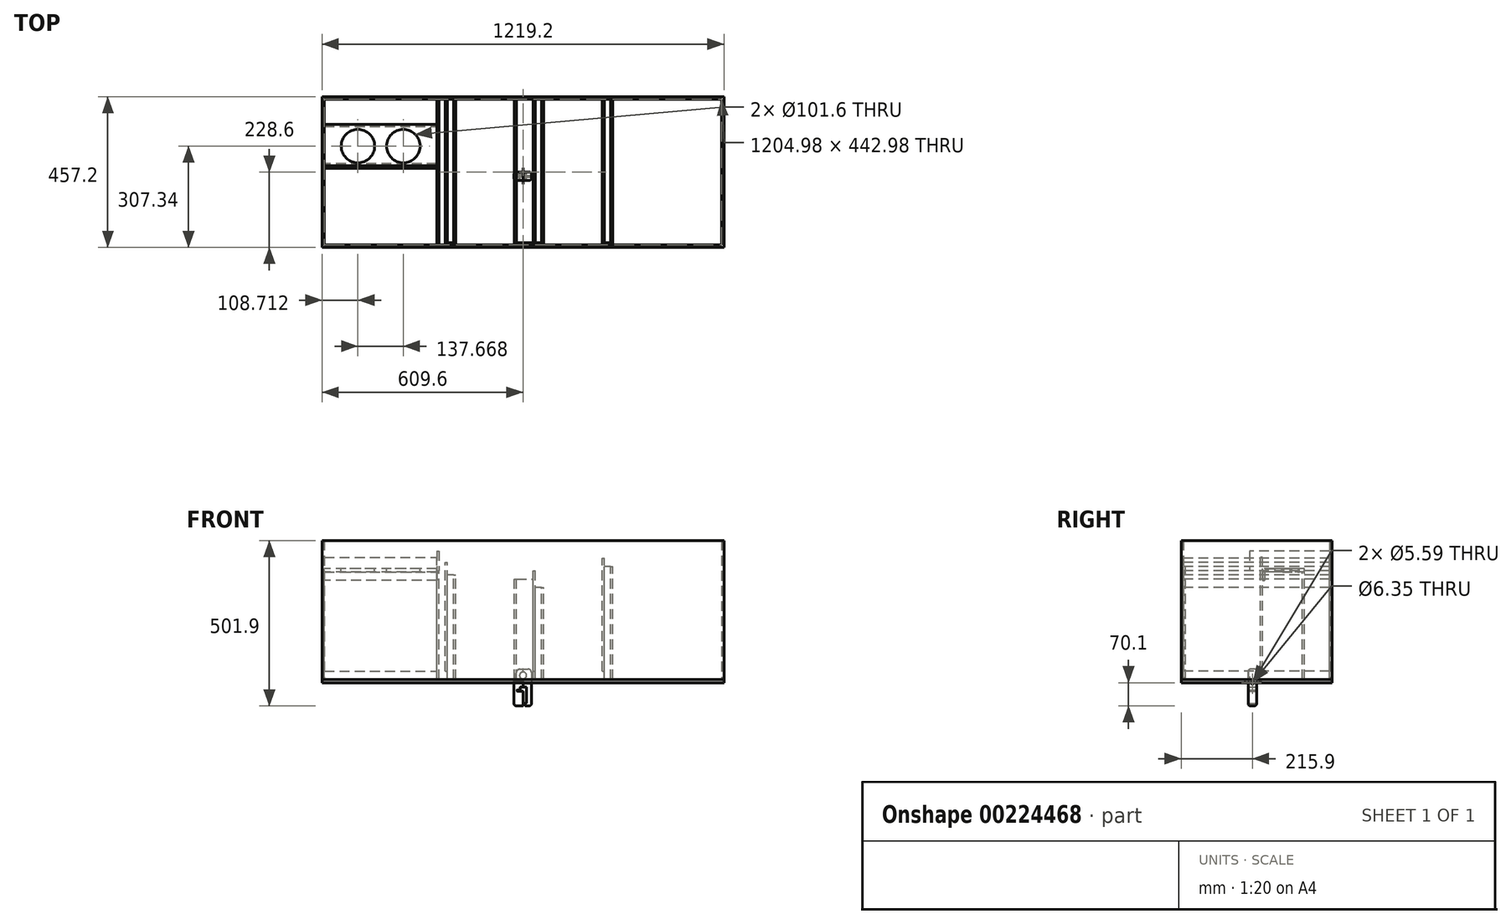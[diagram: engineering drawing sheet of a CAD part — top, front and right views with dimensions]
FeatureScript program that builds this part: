
annotation { "Feature Type Name" : "Feature", "Feature Type Description" : "" }
export const myFeature = defineFeature(function(context is Context, id is Id, definition is map)
    precondition{}
    {
        {
            var Q0;
            Q0=qCreatedBy(makeId("Top.planeOp"),FACE);
            var sketch = newSketch(context, id + "F0", { "sketchPlane" : qUnion([Q0])});
            skLineSegment(sketch, "E0.bottom", {"start": v(-609.6, 228.6) * mm, "end": v(609.6, 228.6) * mm});
            skLineSegment(sketch, "E0.top", {"start": v(-609.6, -228.6) * mm, "end": v(609.6, -228.6) * mm});
            skLineSegment(sketch, "E0.left", {"start": v(-609.6, 228.6) * mm, "end": v(-609.6, -228.6) * mm});
            skLineSegment(sketch, "E0.right", {"start": v(609.6, 228.6) * mm, "end": v(609.6, -228.6) * mm});
            skSolve(sketch);
        }
        {
            var Q0;
            Q0 = qSketchRegion(id + "F0", true);
            extrude(context, id + "F1", {"entities" : qUnion([Q0]), "depth" : 9.65 * mm});
        }
        {
            var Q0;
            Q0=makeQuery(id+"F1.opExtrude","CAP_FACE",FACE,{"disambiguationData":[OSD([sQuery(id+"F0.wireOp",EDGE,"E0.bottom"),sQuery(id+"F0.wireOp",EDGE,"E0.top"),sQuery(id+"F0.wireOp",EDGE,"E0.left"),sQuery(id+"F0.wireOp",EDGE,"E0.right")])],"isStart":false});
            var sketch = newSketch(context, id + "F2", { "sketchPlane" : qUnion([Q0])});
            skLineSegment(sketch, "E1.0", {"start": v(-602.49, 221.49) * mm, "end": v(602.49, 221.49) * mm});
            skLineSegment(sketch, "E1.1", {"start": v(-602.49, 221.49) * mm, "end": v(-602.49, -221.49) * mm});
            skLineSegment(sketch, "E1.2", {"start": v(-602.49, -221.49) * mm, "end": v(602.49, -221.49) * mm});
            skLineSegment(sketch, "E1.3", {"start": v(602.49, 221.49) * mm, "end": v(602.49, -221.49) * mm});
            skLineSegment(sketch, "E2", {"start": v(-609.6, 228.6) * mm, "end": v(609.6, 228.6) * mm});
            skLineSegment(sketch, "E3", {"start": v(609.6, 228.6) * mm, "end": v(609.6, -228.6) * mm});
            skLineSegment(sketch, "E4", {"start": v(609.6, -228.6) * mm, "end": v(-609.6, -228.6) * mm});
            skLineSegment(sketch, "E5", {"start": v(-609.6, -228.6) * mm, "end": v(-609.6, 228.6) * mm});
            skSolve(sketch);
        }
        {
            var Q0;
            Q0 = qSketchRegion(id + "F2", true);
            extrude(context, id + "F3", {"entities" : qUnion([Q0]), "depth" : 422.15 * mm});
        }
        {
            var Q0;
            Q0=makeQuery(id+"F3.opExtrude","CAP_FACE",FACE,{"disambiguationData":[OSD([sQuery(id+"F2.wireOp",EDGE,"E1.0"),sQuery(id+"F2.wireOp",EDGE,"E1.1"),sQuery(id+"F2.wireOp",EDGE,"E1.2"),sQuery(id+"F2.wireOp",EDGE,"E1.3"),sQuery(id+"F2.wireOp",EDGE,"E2"),sQuery(id+"F2.wireOp",EDGE,"E3"),sQuery(id+"F2.wireOp",EDGE,"E4"),sQuery(id+"F2.wireOp",EDGE,"E5")])],"isStart":false});
            var sketch = newSketch(context, id + "F4", { "sketchPlane" : qUnion([Q0])});
            skLineSegment(sketch, "E6", {"start": v(265.94, 221.49) * mm, "end": v(265.94, -221.49) * mm});
            skLineSegment(sketch, "E7", {"start": v(265.94, -221.49) * mm, "end": v(272.29, -221.49) * mm});
            skLineSegment(sketch, "E8", {"start": v(272.29, -221.49) * mm, "end": v(272.29, 221.49) * mm});
            skLineSegment(sketch, "E9", {"start": v(272.29, 221.49) * mm, "end": v(265.94, 221.49) * mm});
            skLineSegment(sketch, "E10", {"start": v(246.89, 221.49) * mm, "end": v(246.89, -221.49) * mm});
            skLineSegment(sketch, "E11", {"start": v(246.89, -221.49) * mm, "end": v(240.54, -221.49) * mm});
            skLineSegment(sketch, "E12", {"start": v(240.54, -221.49) * mm, "end": v(240.54, 221.49) * mm});
            skLineSegment(sketch, "E13", {"start": v(240.54, 221.49) * mm, "end": v(246.89, 221.49) * mm});
            skSolve(sketch);
        }
        {
            var Q0;
            Q0 = qSketchRegion(id + "F4", true);
            extrude(context, id + "F5", {"entities" : qUnion([Q0]), "oppositeDirection" : true, "depth" : 422.15 * mm});
        }
        {
            var Q0;
            Q0=makeQuery(id+"F5.opExtrude","CAP_FACE",FACE,{"disambiguationData":[OSD([sQuery(id+"F4.wireOp",EDGE,"E6"),sQuery(id+"F4.wireOp",EDGE,"E7"),sQuery(id+"F4.wireOp",EDGE,"E8"),sQuery(id+"F4.wireOp",EDGE,"E9")])],"isStart":true});
            var sketch = newSketch(context, id + "F6", { "sketchPlane" : qUnion([Q0])});
            skLineSegment(sketch, "E14.bottom", {"start": v(265.94, 221.49) * mm, "end": v(272.29, 221.49) * mm});
            skLineSegment(sketch, "E14.top", {"start": v(265.94, -221.49) * mm, "end": v(272.29, -221.49) * mm});
            skLineSegment(sketch, "E14.left", {"start": v(265.94, 221.49) * mm, "end": v(265.94, -221.49) * mm});
            skLineSegment(sketch, "E14.right", {"start": v(272.29, 221.49) * mm, "end": v(272.29, -221.49) * mm});
            skSolve(sketch);
        }
        {
            var Q0;
            Q0 = qSketchRegion(id + "F6", true);
            extrude(context, id + "F7", {"entities" : qUnion([Q0]), "operationType" : NewBodyOperationType.REMOVE, "oppositeDirection" : true, "depth" : 79.25 * mm});
        }
        {
            var Q0;
            Q0=makeQuery(id+"F5.opExtrude","CAP_FACE",FACE,{"disambiguationData":[OSD([sQuery(id+"F4.wireOp",EDGE,"E10"),sQuery(id+"F4.wireOp",EDGE,"E11"),sQuery(id+"F4.wireOp",EDGE,"E12"),sQuery(id+"F4.wireOp",EDGE,"E13")])],"isStart":true});
            var sketch = newSketch(context, id + "F8", { "sketchPlane" : qUnion([Q0])});
            skLineSegment(sketch, "E15.bottom", {"start": v(240.54, 221.49) * mm, "end": v(246.89, 221.49) * mm});
            skLineSegment(sketch, "E15.top", {"start": v(240.54, -221.49) * mm, "end": v(246.89, -221.49) * mm});
            skLineSegment(sketch, "E15.left", {"start": v(240.54, 221.49) * mm, "end": v(240.54, -221.49) * mm});
            skLineSegment(sketch, "E15.right", {"start": v(246.89, 221.49) * mm, "end": v(246.89, -221.49) * mm});
            skSolve(sketch);
        }
        {
            var Q0;
            Q0 = qSketchRegion(id + "F8", true);
            extrude(context, id + "F9", {"entities" : qUnion([Q0]), "operationType" : NewBodyOperationType.REMOVE, "oppositeDirection" : true, "depth" : 53.85 * mm});
        }
        {
            var Q0;
            Q0=makeQuery(id+"F5.opExtrude","CAP_FACE",FACE,{"disambiguationData":[OSD([sQuery(id+"F4.wireOp",EDGE,"E10"),sQuery(id+"F4.wireOp",EDGE,"E11"),sQuery(id+"F4.wireOp",EDGE,"E12"),sQuery(id+"F4.wireOp",EDGE,"E13")])],"isStart":false});
            var sketch = newSketch(context, id + "F10", { "sketchPlane" : qUnion([Q0])});
            skLineSegment(sketch, "E16.bottom", {"start": v(240.54, 221.49) * mm, "end": v(246.89, 221.49) * mm});
            skLineSegment(sketch, "E16.top", {"start": v(240.54, -221.49) * mm, "end": v(246.89, -221.49) * mm});
            skLineSegment(sketch, "E16.left", {"start": v(240.54, 221.49) * mm, "end": v(240.54, -221.49) * mm});
            skLineSegment(sketch, "E16.right", {"start": v(246.89, 221.49) * mm, "end": v(246.89, -221.49) * mm});
            skSolve(sketch);
        }
        {
            var Q0;
            Q0 = qSketchRegion(id + "F10", true);
            extrude(context, id + "F11", {"entities" : qUnion([Q0]), "operationType" : NewBodyOperationType.REMOVE, "oppositeDirection" : true, "depth" : 25.4 * mm});
        }
        {
            var Q0;
            Q0=makeQuery(id+"F3.opExtrude","CAP_FACE",FACE,{"disambiguationData":[OSD([sQuery(id+"F2.wireOp",EDGE,"E1.0"),sQuery(id+"F2.wireOp",EDGE,"E1.1"),sQuery(id+"F2.wireOp",EDGE,"E1.2"),sQuery(id+"F2.wireOp",EDGE,"E1.3"),sQuery(id+"F2.wireOp",EDGE,"E2"),sQuery(id+"F2.wireOp",EDGE,"E3"),sQuery(id+"F2.wireOp",EDGE,"E4"),sQuery(id+"F2.wireOp",EDGE,"E5")])],"isStart":false});
            var sketch = newSketch(context, id + "F12", { "sketchPlane" : qUnion([Q0])});
            skLineSegment(sketch, "E17.bottom", {"start": v(56.39, 221.49) * mm, "end": v(62.74, 221.49) * mm});
            skLineSegment(sketch, "E17.top", {"start": v(56.39, -221.49) * mm, "end": v(62.74, -221.49) * mm});
            skLineSegment(sketch, "E17.left", {"start": v(56.39, 221.49) * mm, "end": v(56.39, -221.49) * mm});
            skLineSegment(sketch, "E17.right", {"start": v(62.74, 221.49) * mm, "end": v(62.74, -221.49) * mm});
            skLineSegment(sketch, "E18.bottom", {"start": v(37.34, 221.49) * mm, "end": v(30.99, 221.49) * mm});
            skLineSegment(sketch, "E18.top", {"start": v(37.34, -221.49) * mm, "end": v(30.99, -221.49) * mm});
            skLineSegment(sketch, "E18.left", {"start": v(37.34, 221.49) * mm, "end": v(37.34, -221.49) * mm});
            skLineSegment(sketch, "E18.right", {"start": v(30.99, 221.49) * mm, "end": v(30.99, -221.49) * mm});
            skLineSegment(sketch, "E19.bottom", {"start": v(-26.16, 221.49) * mm, "end": v(-19.81, 221.49) * mm});
            skLineSegment(sketch, "E19.top", {"start": v(-26.16, -221.49) * mm, "end": v(-19.81, -221.49) * mm});
            skLineSegment(sketch, "E19.left", {"start": v(-26.16, 221.49) * mm, "end": v(-26.16, -221.49) * mm});
            skLineSegment(sketch, "E19.right", {"start": v(-19.81, 221.49) * mm, "end": v(-19.81, -221.49) * mm});
            skLineSegment(sketch, "E20.bottom", {"start": v(-210.31, 221.49) * mm, "end": v(-203.96, 221.49) * mm});
            skLineSegment(sketch, "E20.top", {"start": v(-210.31, -221.49) * mm, "end": v(-203.96, -221.49) * mm});
            skLineSegment(sketch, "E20.left", {"start": v(-210.31, 221.49) * mm, "end": v(-210.31, -221.49) * mm});
            skLineSegment(sketch, "E20.right", {"start": v(-203.96, 221.49) * mm, "end": v(-203.96, -221.49) * mm});
            skLineSegment(sketch, "E21.bottom", {"start": v(-235.71, 221.49) * mm, "end": v(-229.36, 221.49) * mm});
            skLineSegment(sketch, "E21.top", {"start": v(-235.71, -221.49) * mm, "end": v(-229.36, -221.49) * mm});
            skLineSegment(sketch, "E21.left", {"start": v(-235.71, 221.49) * mm, "end": v(-235.71, -221.49) * mm});
            skLineSegment(sketch, "E21.right", {"start": v(-229.36, 221.49) * mm, "end": v(-229.36, -221.49) * mm});
            skLineSegment(sketch, "E22.bottom", {"start": v(-261.11, 221.49) * mm, "end": v(-254.76, 221.49) * mm});
            skLineSegment(sketch, "E22.top", {"start": v(-261.11, -221.49) * mm, "end": v(-254.76, -221.49) * mm});
            skLineSegment(sketch, "E22.left", {"start": v(-261.11, 221.49) * mm, "end": v(-261.11, -221.49) * mm});
            skLineSegment(sketch, "E22.right", {"start": v(-254.76, 221.49) * mm, "end": v(-254.76, -221.49) * mm});
            skSolve(sketch);
        }
        {
            var Q0;
            Q0 = qSketchRegion(id + "F12", true);
            extrude(context, id + "F13", {"entities" : qUnion([Q0]), "oppositeDirection" : true, "depth" : 422.15 * mm});
        }
        {
            var Q0;
            Q0=makeQuery(id+"F13.opExtrude","CAP_FACE",FACE,{"disambiguationData":[OSD([sQuery(id+"F12.wireOp",EDGE,"E17.bottom"),sQuery(id+"F12.wireOp",EDGE,"E17.top"),sQuery(id+"F12.wireOp",EDGE,"E17.left"),sQuery(id+"F12.wireOp",EDGE,"E17.right")])],"isStart":true});
            var sketch = newSketch(context, id + "F14", { "sketchPlane" : qUnion([Q0])});
            skLineSegment(sketch, "E23.bottom", {"start": v(56.39, 221.49) * mm, "end": v(62.74, 221.49) * mm});
            skLineSegment(sketch, "E23.top", {"start": v(56.39, -221.49) * mm, "end": v(62.74, -221.49) * mm});
            skLineSegment(sketch, "E23.left", {"start": v(56.39, 221.49) * mm, "end": v(56.39, -221.49) * mm});
            skLineSegment(sketch, "E23.right", {"start": v(62.74, 221.49) * mm, "end": v(62.74, -221.49) * mm});
            skSolve(sketch);
        }
        {
            var Q0;
            Q0 = qSketchRegion(id + "F14", true);
            extrude(context, id + "F15", {"entities" : qUnion([Q0]), "operationType" : NewBodyOperationType.REMOVE, "oppositeDirection" : true, "depth" : 142.75 * mm});
        }
        {
            var Q0;
            Q0=makeQuery(id+"F13.opExtrude","CAP_FACE",FACE,{"disambiguationData":[OSD([sQuery(id+"F12.wireOp",EDGE,"E18.bottom"),sQuery(id+"F12.wireOp",EDGE,"E18.top"),sQuery(id+"F12.wireOp",EDGE,"E18.left"),sQuery(id+"F12.wireOp",EDGE,"E18.right")])],"isStart":true});
            var sketch = newSketch(context, id + "F16", { "sketchPlane" : qUnion([Q0])});
            skLineSegment(sketch, "E24.bottom", {"start": v(30.99, 221.49) * mm, "end": v(37.34, 221.49) * mm});
            skLineSegment(sketch, "E24.top", {"start": v(30.99, -221.49) * mm, "end": v(37.34, -221.49) * mm});
            skLineSegment(sketch, "E24.left", {"start": v(30.99, 221.49) * mm, "end": v(30.99, -221.49) * mm});
            skLineSegment(sketch, "E24.right", {"start": v(37.34, 221.49) * mm, "end": v(37.34, -221.49) * mm});
            skSolve(sketch);
        }
        {
            var Q0;
            Q0 = qSketchRegion(id + "F16", true);
            extrude(context, id + "F17", {"entities" : qUnion([Q0]), "operationType" : NewBodyOperationType.REMOVE, "oppositeDirection" : true, "depth" : 91.95 * mm});
        }
        {
            var Q0;
            Q0=makeQuery(id+"F13.opExtrude","CAP_FACE",FACE,{"disambiguationData":[OSD([sQuery(id+"F12.wireOp",EDGE,"E19.bottom"),sQuery(id+"F12.wireOp",EDGE,"E19.top"),sQuery(id+"F12.wireOp",EDGE,"E19.left"),sQuery(id+"F12.wireOp",EDGE,"E19.right")])],"isStart":true});
            var sketch = newSketch(context, id + "F18", { "sketchPlane" : qUnion([Q0])});
            skLineSegment(sketch, "E25.bottom", {"start": v(-26.16, 221.49) * mm, "end": v(-19.81, 221.49) * mm});
            skLineSegment(sketch, "E25.top", {"start": v(-26.16, -221.49) * mm, "end": v(-19.81, -221.49) * mm});
            skLineSegment(sketch, "E25.left", {"start": v(-26.16, 221.49) * mm, "end": v(-26.16, -221.49) * mm});
            skLineSegment(sketch, "E25.right", {"start": v(-19.81, 221.49) * mm, "end": v(-19.81, -221.49) * mm});
            skSolve(sketch);
        }
        {
            var Q0;
            Q0 = qSketchRegion(id + "F18", true);
            extrude(context, id + "F19", {"entities" : qUnion([Q0]), "operationType" : NewBodyOperationType.REMOVE, "oppositeDirection" : true, "depth" : 117.35 * mm});
        }
        {
            var Q0;
            Q0=makeQuery(id+"F13.opExtrude","CAP_FACE",FACE,{"disambiguationData":[OSD([sQuery(id+"F12.wireOp",EDGE,"E18.bottom"),sQuery(id+"F12.wireOp",EDGE,"E18.top"),sQuery(id+"F12.wireOp",EDGE,"E18.left"),sQuery(id+"F12.wireOp",EDGE,"E18.right")])],"isStart":false});
            var sketch = newSketch(context, id + "F20", { "sketchPlane" : qUnion([Q0])});
            skLineSegment(sketch, "E26.bottom", {"start": v(30.99, 221.49) * mm, "end": v(37.34, 221.49) * mm});
            skLineSegment(sketch, "E26.top", {"start": v(30.99, -221.49) * mm, "end": v(37.34, -221.49) * mm});
            skLineSegment(sketch, "E26.left", {"start": v(30.99, 221.49) * mm, "end": v(30.99, -221.49) * mm});
            skLineSegment(sketch, "E26.right", {"start": v(37.34, 221.49) * mm, "end": v(37.34, -221.49) * mm});
            skSolve(sketch);
        }
        {
            var Q0;
            Q0 = qSketchRegion(id + "F20", true);
            extrude(context, id + "F21", {"entities" : qUnion([Q0]), "operationType" : NewBodyOperationType.REMOVE, "oppositeDirection" : true, "depth" : 25.4 * mm});
        }
        {
            var Q0;
            Q0=makeQuery(id+"F13.opExtrude","CAP_FACE",FACE,{"disambiguationData":[OSD([sQuery(id+"F12.wireOp",EDGE,"E20.bottom"),sQuery(id+"F12.wireOp",EDGE,"E20.top"),sQuery(id+"F12.wireOp",EDGE,"E20.left"),sQuery(id+"F12.wireOp",EDGE,"E20.right")])],"isStart":true});
            var sketch = newSketch(context, id + "F22", { "sketchPlane" : qUnion([Q0])});
            skLineSegment(sketch, "E27.bottom", {"start": v(-210.31, 221.49) * mm, "end": v(-203.96, 221.49) * mm});
            skLineSegment(sketch, "E27.top", {"start": v(-210.31, -221.49) * mm, "end": v(-203.96, -221.49) * mm});
            skLineSegment(sketch, "E27.left", {"start": v(-210.31, 221.49) * mm, "end": v(-210.31, -221.49) * mm});
            skLineSegment(sketch, "E27.right", {"start": v(-203.96, 221.49) * mm, "end": v(-203.96, -221.49) * mm});
            skSolve(sketch);
        }
        {
            var Q0;
            Q0 = qSketchRegion(id + "F22", true);
            extrude(context, id + "F23", {"entities" : qUnion([Q0]), "operationType" : NewBodyOperationType.REMOVE, "oppositeDirection" : true, "depth" : 104.65 * mm});
        }
        {
            var Q0;
            Q0=makeQuery(id+"F13.opExtrude","CAP_FACE",FACE,{"disambiguationData":[OSD([sQuery(id+"F12.wireOp",EDGE,"E21.bottom"),sQuery(id+"F12.wireOp",EDGE,"E21.top"),sQuery(id+"F12.wireOp",EDGE,"E21.left"),sQuery(id+"F12.wireOp",EDGE,"E21.right")])],"isStart":true});
            var sketch = newSketch(context, id + "F24", { "sketchPlane" : qUnion([Q0])});
            skLineSegment(sketch, "E28.bottom", {"start": v(-235.71, 221.49) * mm, "end": v(-229.36, 221.49) * mm});
            skLineSegment(sketch, "E28.top", {"start": v(-235.71, -221.49) * mm, "end": v(-229.36, -221.49) * mm});
            skLineSegment(sketch, "E28.left", {"start": v(-235.71, 221.49) * mm, "end": v(-235.71, -221.49) * mm});
            skLineSegment(sketch, "E28.right", {"start": v(-229.36, 221.49) * mm, "end": v(-229.36, -221.49) * mm});
            skSolve(sketch);
        }
        {
            var Q0;
            Q0 = qSketchRegion(id + "F24", true);
            extrude(context, id + "F25", {"entities" : qUnion([Q0]), "operationType" : NewBodyOperationType.REMOVE, "oppositeDirection" : true, "depth" : 66.55 * mm});
        }
        {
            var Q0;
            Q0=makeQuery(id+"F13.opExtrude","CAP_FACE",FACE,{"disambiguationData":[OSD([sQuery(id+"F12.wireOp",EDGE,"E22.bottom"),sQuery(id+"F12.wireOp",EDGE,"E22.top"),sQuery(id+"F12.wireOp",EDGE,"E22.left"),sQuery(id+"F12.wireOp",EDGE,"E22.right")])],"isStart":true});
            var sketch = newSketch(context, id + "F26", { "sketchPlane" : qUnion([Q0])});
            skLineSegment(sketch, "E29.bottom", {"start": v(-261.11, 221.49) * mm, "end": v(-254.76, 221.49) * mm});
            skLineSegment(sketch, "E29.top", {"start": v(-261.11, -221.49) * mm, "end": v(-254.76, -221.49) * mm});
            skLineSegment(sketch, "E29.left", {"start": v(-261.11, 221.49) * mm, "end": v(-261.11, -221.49) * mm});
            skLineSegment(sketch, "E29.right", {"start": v(-254.76, 221.49) * mm, "end": v(-254.76, -221.49) * mm});
            skSolve(sketch);
        }
        {
            var Q0;
            Q0 = qSketchRegion(id + "F26", true);
            extrude(context, id + "F27", {"entities" : qUnion([Q0]), "operationType" : NewBodyOperationType.REMOVE, "oppositeDirection" : true, "depth" : 91.95 * mm});
        }
        {
            var Q0;
            Q0=makeQuery(id+"F3.opExtrude","CAP_FACE",FACE,{"disambiguationData":[OSD([sQuery(id+"F2.wireOp",EDGE,"E1.0"),sQuery(id+"F2.wireOp",EDGE,"E1.1"),sQuery(id+"F2.wireOp",EDGE,"E1.2"),sQuery(id+"F2.wireOp",EDGE,"E1.3"),sQuery(id+"F2.wireOp",EDGE,"E2"),sQuery(id+"F2.wireOp",EDGE,"E3"),sQuery(id+"F2.wireOp",EDGE,"E4"),sQuery(id+"F2.wireOp",EDGE,"E5")])],"isStart":false});
            var sketch = newSketch(context, id + "F28", { "sketchPlane" : qUnion([Q0])});
            skLineSegment(sketch, "E30.bottom", {"start": v(-602.49, 145.29) * mm, "end": v(-261.5, 145.29) * mm});
            skLineSegment(sketch, "E30.top", {"start": v(-602.49, 138.94) * mm, "end": v(-261.5, 138.94) * mm});
            skLineSegment(sketch, "E30.left", {"start": v(-602.49, 145.29) * mm, "end": v(-602.49, 138.94) * mm});
            skLineSegment(sketch, "E30.right", {"start": v(-261.5, 145.29) * mm, "end": v(-261.5, 138.94) * mm});
            skLineSegment(sketch, "E31.bottom", {"start": v(-602.49, 18.29) * mm, "end": v(-261.5, 18.29) * mm});
            skLineSegment(sketch, "E31.top", {"start": v(-602.49, 11.94) * mm, "end": v(-261.5, 11.94) * mm});
            skLineSegment(sketch, "E31.left", {"start": v(-602.49, 18.29) * mm, "end": v(-602.49, 11.94) * mm});
            skLineSegment(sketch, "E31.right", {"start": v(-261.5, 18.29) * mm, "end": v(-261.5, 11.94) * mm});
            skSolve(sketch);
        }
        {
            var Q0;
            Q0 = qSketchRegion(id + "F28", true);
            extrude(context, id + "F29", {"entities" : qUnion([Q0]), "oppositeDirection" : true, "depth" : 422.15 * mm});
        }
        {
            var Q0;
            Q0=makeQuery(id+"F13.opExtrude","CAP_FACE",FACE,{"disambiguationData":[OSD([sQuery(id+"F12.wireOp",EDGE,"E21.bottom"),sQuery(id+"F12.wireOp",EDGE,"E21.top"),sQuery(id+"F12.wireOp",EDGE,"E21.left"),sQuery(id+"F12.wireOp",EDGE,"E21.right")])],"isStart":false});
            var sketch = newSketch(context, id + "F30", { "sketchPlane" : qUnion([Q0])});
            skLineSegment(sketch, "E32.bottom", {"start": v(-235.71, 221.49) * mm, "end": v(-229.36, 221.49) * mm});
            skLineSegment(sketch, "E32.top", {"start": v(-235.71, -221.49) * mm, "end": v(-229.36, -221.49) * mm});
            skLineSegment(sketch, "E32.left", {"start": v(-235.71, 221.49) * mm, "end": v(-235.71, -221.49) * mm});
            skLineSegment(sketch, "E32.right", {"start": v(-229.36, 221.49) * mm, "end": v(-229.36, -221.49) * mm});
            skSolve(sketch);
        }
        {
            var Q0;
            Q0 = qSketchRegion(id + "F30", true);
            extrude(context, id + "F31", {"entities" : qUnion([Q0]), "operationType" : NewBodyOperationType.REMOVE, "oppositeDirection" : true, "depth" : 25.4 * mm});
        }
        {
            var Q0;
            Q0=makeQuery(id+"F29.opExtrude","CAP_FACE",FACE,{"disambiguationData":[OSD([sQuery(id+"F28.wireOp",EDGE,"E31.bottom"),sQuery(id+"F28.wireOp",EDGE,"E31.top"),sQuery(id+"F28.wireOp",EDGE,"E31.left"),sQuery(id+"F28.wireOp",EDGE,"E31.right")])],"isStart":false});
            var sketch = newSketch(context, id + "F32", { "sketchPlane" : qUnion([Q0])});
            skLineSegment(sketch, "E33.bottom", {"start": v(-602.49, -11.94) * mm, "end": v(-261.5, -11.94) * mm});
            skLineSegment(sketch, "E33.top", {"start": v(-602.49, -18.29) * mm, "end": v(-261.5, -18.29) * mm});
            skLineSegment(sketch, "E33.left", {"start": v(-602.49, -11.94) * mm, "end": v(-602.49, -18.29) * mm});
            skLineSegment(sketch, "E33.right", {"start": v(-261.5, -11.94) * mm, "end": v(-261.5, -18.29) * mm});
            skSolve(sketch);
        }
        {
            var Q0;
            Q0 = qSketchRegion(id + "F32", true);
            extrude(context, id + "F33", {"entities" : qUnion([Q0]), "operationType" : NewBodyOperationType.REMOVE, "oppositeDirection" : true, "depth" : 25.4 * mm});
        }
        {
            var Q0;
            Q0=makeQuery(id+"F29.opExtrude","CAP_FACE",FACE,{"disambiguationData":[OSD([sQuery(id+"F28.wireOp",EDGE,"E30.bottom"),sQuery(id+"F28.wireOp",EDGE,"E30.top"),sQuery(id+"F28.wireOp",EDGE,"E30.left"),sQuery(id+"F28.wireOp",EDGE,"E30.right")])],"isStart":true});
            var sketch = newSketch(context, id + "F34", { "sketchPlane" : qUnion([Q0])});
            skLineSegment(sketch, "E34.bottom", {"start": v(-602.49, 145.29) * mm, "end": v(-261.5, 145.29) * mm});
            skLineSegment(sketch, "E34.top", {"start": v(-602.49, 138.94) * mm, "end": v(-261.5, 138.94) * mm});
            skLineSegment(sketch, "E34.left", {"start": v(-602.49, 145.29) * mm, "end": v(-602.49, 138.94) * mm});
            skLineSegment(sketch, "E34.right", {"start": v(-261.5, 145.29) * mm, "end": v(-261.5, 138.94) * mm});
            skSolve(sketch);
        }
        {
            var Q0;
            Q0 = qSketchRegion(id + "F34", true);
            extrude(context, id + "F35", {"entities" : qUnion([Q0]), "operationType" : NewBodyOperationType.REMOVE, "oppositeDirection" : true, "depth" : 95.25 * mm});
        }
        {
            var Q0;
            Q0=makeQuery(id+"F29.opExtrude","CAP_FACE",FACE,{"disambiguationData":[OSD([sQuery(id+"F28.wireOp",EDGE,"E31.bottom"),sQuery(id+"F28.wireOp",EDGE,"E31.top"),sQuery(id+"F28.wireOp",EDGE,"E31.left"),sQuery(id+"F28.wireOp",EDGE,"E31.right")])],"isStart":true});
            var sketch = newSketch(context, id + "F36", { "sketchPlane" : qUnion([Q0])});
            skLineSegment(sketch, "E35.bottom", {"start": v(-602.49, 18.29) * mm, "end": v(-261.5, 18.29) * mm});
            skLineSegment(sketch, "E35.top", {"start": v(-602.49, 11.94) * mm, "end": v(-261.5, 11.94) * mm});
            skLineSegment(sketch, "E35.left", {"start": v(-602.49, 18.29) * mm, "end": v(-602.49, 11.94) * mm});
            skLineSegment(sketch, "E35.right", {"start": v(-261.5, 18.29) * mm, "end": v(-261.5, 11.94) * mm});
            skSolve(sketch);
        }
        {
            var Q0;
            Q0 = qSketchRegion(id + "F36", true);
            extrude(context, id + "F37", {"entities" : qUnion([Q0]), "operationType" : NewBodyOperationType.REMOVE, "oppositeDirection" : true, "depth" : 50.8 * mm});
        }
        {
            var Q0;
            Q0=makeQuery(id+"F27.boolean.opBoolean","COPY",FACE,{"derivedFrom":makeQuery(id+"F27.opExtrude","CAP_FACE",FACE,{"disambiguationData":[OSD([sQuery(id+"F26.wireOp",EDGE,"E29.bottom"),sQuery(id+"F26.wireOp",EDGE,"E29.top"),sQuery(id+"F26.wireOp",EDGE,"E29.left"),sQuery(id+"F26.wireOp",EDGE,"E29.right")])],"isStart":false})});
            var sketch = newSketch(context, id + "F38", { "sketchPlane" : qUnion([Q0])});
            skLineSegment(sketch, "E36.bottom", {"start": v(-261.11, 221.49) * mm, "end": v(-254.76, 221.49) * mm});
            skLineSegment(sketch, "E36.top", {"start": v(-261.11, -21.6) * mm, "end": v(-254.76, -21.6) * mm});
            skLineSegment(sketch, "E36.left", {"start": v(-261.11, 221.49) * mm, "end": v(-261.11, -21.6) * mm});
            skLineSegment(sketch, "E36.right", {"start": v(-254.76, 221.49) * mm, "end": v(-254.76, -21.6) * mm});
            skSolve(sketch);
        }
        {
            var Q0;
            Q0 = qSketchRegion(id + "F38", true);
            extrude(context, id + "F39", {"entities" : qUnion([Q0]), "depth" : 60.45 * mm});
        }
        {
            var Q0;
            Q0=makeQuery(id+"F29.opExtrude","SWEPT_FACE",FACE,{"disambiguationData":[OSD([sQuery(id+"F28.wireOp",EDGE,"E30.left")])]});
            var sketch = newSketch(context, id + "F40", { "sketchPlane" : qUnion([Q0])});
            skLineSegment(sketch, "E37.bottom", {"start": v(-145.29, 336.55) * mm, "end": v(-18.35, 336.55) * mm});
            skLineSegment(sketch, "E37.top", {"start": v(-145.29, 346.2) * mm, "end": v(-18.35, 346.2) * mm});
            skLineSegment(sketch, "E37.left", {"start": v(-145.29, 336.55) * mm, "end": v(-145.29, 346.2) * mm});
            skLineSegment(sketch, "E37.right", {"start": v(-18.35, 336.55) * mm, "end": v(-18.35, 346.2) * mm});
            skSolve(sketch);
        }
        {
            var Q0;
            Q0 = qSketchRegion(id + "F40", true);
            extrude(context, id + "F41", {"entities" : qUnion([Q0]), "oppositeDirection" : true, "depth" : 340.87 * mm});
        }
        {
            var Q0;
            Q0=makeQuery(id+"F41.opExtrude","SWEPT_FACE",FACE,{"disambiguationData":[OSD([sQuery(id+"F40.wireOp",EDGE,"E37.top")])]});
            var sketch = newSketch(context, id + "F42", { "sketchPlane" : qUnion([Q0])});
            skCircle(sketch, "E38", {"center": v(-500.89, 78.74) * mm, "radius": 50.8 * mm});
            skCircle(sketch, "E39", {"center": v(-363.22, 78.74) * mm, "radius": 50.8 * mm});
            skSolve(sketch);
        }
        {
            var Q0;
            Q0 = qSketchRegion(id + "F42", true);
            extrude(context, id + "F43", {"entities" : qUnion([Q0]), "operationType" : NewBodyOperationType.REMOVE, "oppositeDirection" : true, "depth" : 25.4 * mm});
        }
        {
            var Q0;
            Q0=makeQuery(id+"F23.boolean.opBoolean","COPY",FACE,{"derivedFrom":makeQuery(id+"F23.opExtrude","CAP_FACE",FACE,{"disambiguationData":[OSD([sQuery(id+"F22.wireOp",EDGE,"E27.bottom"),sQuery(id+"F22.wireOp",EDGE,"E27.top"),sQuery(id+"F22.wireOp",EDGE,"E27.left"),sQuery(id+"F22.wireOp",EDGE,"E27.right")])],"isStart":false})});
            var sketch = newSketch(context, id + "F44", { "sketchPlane" : qUnion([Q0])});
            skLineSegment(sketch, "E40.bottom", {"start": v(-210.31, -221.49) * mm, "end": v(-229.36, -221.49) * mm});
            skLineSegment(sketch, "E40.top", {"start": v(-210.31, -215.14) * mm, "end": v(-229.36, -215.14) * mm});
            skLineSegment(sketch, "E40.left", {"start": v(-210.31, -221.49) * mm, "end": v(-210.31, -215.14) * mm});
            skLineSegment(sketch, "E40.right", {"start": v(-229.36, -221.49) * mm, "end": v(-229.36, -215.14) * mm});
            skSolve(sketch);
        }
        {
            var Q0;
            Q0 = qSketchRegion(id + "F44", true);
            extrude(context, id + "F45", {"entities" : qUnion([Q0]), "oppositeDirection" : true, "depth" : 317.5 * mm});
        }
        {
            var Q0;
            Q0=makeQuery(id+"F7.boolean.opBoolean","COPY",FACE,{"derivedFrom":makeQuery(id+"F7.opExtrude","CAP_FACE",FACE,{"disambiguationData":[OSD([sQuery(id+"F6.wireOp",EDGE,"E14.bottom"),sQuery(id+"F6.wireOp",EDGE,"E14.top"),sQuery(id+"F6.wireOp",EDGE,"E14.left"),sQuery(id+"F6.wireOp",EDGE,"E14.right")])],"isStart":false})});
            var sketch = newSketch(context, id + "F46", { "sketchPlane" : qUnion([Q0])});
            skLineSegment(sketch, "E41.bottom", {"start": v(265.94, -221.49) * mm, "end": v(246.89, -221.49) * mm});
            skLineSegment(sketch, "E41.top", {"start": v(265.94, -215.14) * mm, "end": v(246.89, -215.14) * mm});
            skLineSegment(sketch, "E41.left", {"start": v(265.94, -221.49) * mm, "end": v(265.94, -215.14) * mm});
            skLineSegment(sketch, "E41.right", {"start": v(246.89, -221.49) * mm, "end": v(246.89, -215.14) * mm});
            skSolve(sketch);
        }
        {
            var Q0;
            Q0 = qSketchRegion(id + "F46", true);
            extrude(context, id + "F47", {"entities" : qUnion([Q0]), "oppositeDirection" : true, "depth" : 342.9 * mm});
        }
        {
            var Q0;
            Q0=makeQuery(id+"F15.boolean.opBoolean","COPY",FACE,{"derivedFrom":makeQuery(id+"F15.opExtrude","CAP_FACE",FACE,{"disambiguationData":[OSD([sQuery(id+"F14.wireOp",EDGE,"E23.bottom"),sQuery(id+"F14.wireOp",EDGE,"E23.top"),sQuery(id+"F14.wireOp",EDGE,"E23.left"),sQuery(id+"F14.wireOp",EDGE,"E23.right")])],"isStart":false})});
            var sketch = newSketch(context, id + "F48", { "sketchPlane" : qUnion([Q0])});
            skLineSegment(sketch, "E42.bottom", {"start": v(56.39, -221.49) * mm, "end": v(37.34, -221.49) * mm});
            skLineSegment(sketch, "E42.top", {"start": v(56.39, -215.14) * mm, "end": v(37.34, -215.14) * mm});
            skLineSegment(sketch, "E42.left", {"start": v(56.39, -221.49) * mm, "end": v(56.39, -215.14) * mm});
            skLineSegment(sketch, "E42.right", {"start": v(37.34, -221.49) * mm, "end": v(37.34, -215.14) * mm});
            skSolve(sketch);
        }
        {
            var Q0;
            Q0 = qSketchRegion(id + "F48", true);
            extrude(context, id + "F49", {"entities" : qUnion([Q0]), "oppositeDirection" : true, "depth" : 279.4 * mm});
        }
        {
            var Q0;
            Q0=makeQuery(id+"F19.boolean.opBoolean","COPY",FACE,{"derivedFrom":makeQuery(id+"F19.opExtrude","CAP_FACE",FACE,{"disambiguationData":[OSD([sQuery(id+"F18.wireOp",EDGE,"E25.bottom"),sQuery(id+"F18.wireOp",EDGE,"E25.top"),sQuery(id+"F18.wireOp",EDGE,"E25.left"),sQuery(id+"F18.wireOp",EDGE,"E25.right")])],"isStart":false})});
            var sketch = newSketch(context, id + "F50", { "sketchPlane" : qUnion([Q0])});
            skLineSegment(sketch, "E43.bottom", {"start": v(-19.81, -221.49) * mm, "end": v(30.99, -221.49) * mm});
            skLineSegment(sketch, "E43.top", {"start": v(-19.81, -215.14) * mm, "end": v(30.99, -215.14) * mm});
            skLineSegment(sketch, "E43.left", {"start": v(-19.81, -221.49) * mm, "end": v(-19.81, -215.14) * mm});
            skLineSegment(sketch, "E43.right", {"start": v(30.99, -221.49) * mm, "end": v(30.99, -215.14) * mm});
            skSolve(sketch);
        }
        {
            var Q0;
            Q0 = qSketchRegion(id + "F50", true);
            extrude(context, id + "F51", {"entities" : qUnion([Q0]), "oppositeDirection" : true, "depth" : 304.8 * mm});
        }
        {
            var Q0;
            Q0=makeQuery(id+"F41.opExtrude","CAP_FACE",FACE,{"disambiguationData":[OSD([sQuery(id+"F40.wireOp",EDGE,"E37.bottom"),sQuery(id+"F40.wireOp",EDGE,"E37.top"),sQuery(id+"F40.wireOp",EDGE,"E37.left"),sQuery(id+"F40.wireOp",EDGE,"E37.right")])],"isStart":true});
            var sketch = newSketch(context, id + "F52", { "sketchPlane" : qUnion([Q0])});
            skLineSegment(sketch, "E44.bottom", {"start": v(-18.35, 336.55) * mm, "end": v(-24.7, 336.55) * mm});
            skLineSegment(sketch, "E44.top", {"start": v(-18.35, 311.15) * mm, "end": v(-24.7, 311.15) * mm});
            skLineSegment(sketch, "E44.left", {"start": v(-18.35, 336.55) * mm, "end": v(-18.35, 311.15) * mm});
            skLineSegment(sketch, "E44.right", {"start": v(-24.7, 336.55) * mm, "end": v(-24.7, 311.15) * mm});
            skSolve(sketch);
        }
        {
            var Q0;
            Q0 = qSketchRegion(id + "F52", true);
            extrude(context, id + "F53", {"entities" : qUnion([Q0]), "oppositeDirection" : true, "depth" : 340.87 * mm});
        }
        {
            var Q0;
            Q0=qCreatedBy(makeId("Front.planeOp"),FACE);
            var sketch = newSketch(context, id + "F54", { "sketchPlane" : qUnion([Q0])});
            skLineSegment(sketch, "E45.bottom", {"start": v(-9.53, 41.15) * mm, "end": v(15.87, 41.15) * mm});
            skLineSegment(sketch, "E45.top", {"start": v(-27.3, -69.85) * mm, "end": v(0, -69.85) * mm});
            skLineSegment(sketch, "E45.left", {"start": v(-27.3, 15.9) * mm, "end": v(-27.3, -69.85) * mm});
            skLineSegment(sketch, "E45.right", {"start": v(25.4, 31.62) * mm, "end": v(25.4, -70.1) * mm});
            skCircle(sketch, "E46", {"center": v(0, 22.1) * mm, "radius": 10.67 * mm});
            skLineSegment(sketch, "E47.left", {"start": v(0, -69.85) * mm, "end": v(0, -26.13) * mm});
            skLineSegment(sketch, "E47.right", {"start": v(9.9, -62.23) * mm, "end": v(9.9, -12.7) * mm});
            skLineSegment(sketch, "E48", {"start": v(-8.64, -12.7) * mm, "end": v(-8.64, -21.34) * mm});
            skLineSegment(sketch, "E49.trimOffspring", {"start": v(0, -26.13) * mm, "end": v(0, -69.85) * mm});
            skArc(sketch, "E50", {"start": v(25.4, 31.62) * mm, "mid": v(22.61, 38.36) * mm, "end": v(15.87, 41.15) * mm});
            skPoint(sketch, "E51.orphan", {"position": v(25.4, 41.15) * mm});
            skLineSegment(sketch, "E52", {"start": v(-8.64, -21.34) * mm, "end": v(-17.78, -21.34) * mm});
            skLineSegment(sketch, "E53", {"start": v(-17.78, -21.34) * mm, "end": v(-17.78, -26.13) * mm});
            skLineSegment(sketch, "E54", {"start": v(-17.78, -26.13) * mm, "end": v(0, -26.13) * mm});
            skPoint(sketch, "E55.start.orphan", {"position": v(-3.18, 38.1) * mm});
            skLineSegment(sketch, "E56", {"start": v(-8.64, -12.7) * mm, "end": v(9.9, -12.7) * mm});
            skLineSegment(sketch, "E57", {"start": v(6.35, -70.1) * mm, "end": v(6.35, -62.23) * mm});
            skLineSegment(sketch, "E58", {"start": v(6.35, -62.23) * mm, "end": v(9.9, -62.23) * mm});
            skLineSegment(sketch, "E59.trimOffspring", {"start": v(0, 32.77) * mm, "end": v(0, 41.15) * mm});
            skLineSegment(sketch, "E60.trimOffspring", {"start": v(0, -12.7) * mm, "end": v(0, 11.43) * mm});
            skLineSegment(sketch, "E61", {"start": v(25.4, -70.1) * mm, "end": v(6.35, -70.1) * mm});
            skArc(sketch, "E62", {"start": v(-9.53, 41.15) * mm, "mid": v(-15.28, 39.21) * mm, "end": v(-18.7, 34.2) * mm});
            skLineSegment(sketch, "E63", {"start": v(-26.8, 18.04) * mm, "end": v(-18.7, 34.2) * mm});
            skArc(sketch, "E64", {"start": v(-26.8, 18.04) * mm, "mid": v(-27.18, 17) * mm, "end": v(-27.3, 15.9) * mm});
            skSolve(sketch);
        }
        {
            var Q0;
            {var subQ5=sQuery(id+"F54.wireOp",EDGE,"E45.right");Q0=makeQuery(id+"F54.imprint","IMPRINT",FACE,{"disambiguationData":[TD([[makeQuery(id+"F54.imprint","IMPRINT",EDGE,{"derivedFrom":subQ5}),-1.0]])]});}
            extrude(context, id + "F55", {"entities" : qUnion([Q0]), "depth" : 25.4 * mm});
        }
        {
            var Q0;
            Q0=makeQuery(id+"F54.imprint","IMPRINT",FACE,{"disambiguationData":[TD([[makeQuery(id+"F54.imprint","IMPRINT",EDGE,{"derivedFrom":sQuery(id+"F54.wireOp",EDGE,"E45.top")}),1.0]])]});
            extrude(context, id + "F56", {"entities" : qUnion([Q0]), "depth" : 25.4 * mm});
        }
        {
            var Q0;
            Q0=makeQuery(id+"F56.opExtrude","SWEPT_FACE",FACE,{"disambiguationData":[OSD([sQuery(id+"F54.wireOp",EDGE,"E45.left")])]});
            var Q1;
            Q1=makeQuery(id+"F55.opExtrude","SWEPT_FACE",FACE,{"disambiguationData":[OSD([sQuery(id+"F54.wireOp",EDGE,"E45.right")])]});
            var Q2;
            Q2=makeQuery(id+"F56.opExtrude","CAP_EDGE",EDGE,{"disambiguationData":[OSD([sQuery(id+"F54.wireOp",EDGE,"E45.top")])],"isStart":false});
            var Q3;
            Q3=makeQuery(id+"F55.opExtrude","CAP_EDGE",EDGE,{"disambiguationData":[OSD([sQuery(id+"F54.wireOp",EDGE,"E61")])],"isStart":false});
            var Q4;
            Q4=makeQuery(id+"F56.opExtrude","CAP_EDGE",EDGE,{"disambiguationData":[OSD([sQuery(id+"F54.wireOp",EDGE,"E45.top")])],"isStart":true});
            var Q5;
            Q5=makeQuery(id+"F55.opExtrude","CAP_EDGE",EDGE,{"disambiguationData":[OSD([sQuery(id+"F54.wireOp",EDGE,"E61")])],"isStart":true});
            var Q6;
            Q6=makeQuery(id+"F56.opExtrude","SWEPT_FACE",FACE,{"disambiguationData":[OSD([sQuery(id+"F54.wireOp",EDGE,"E62")])]});
            fillet(context, id + "F57", {"entities" : qUnion([Q0, Q1, Q2, Q3, Q4, Q5, Q6]), "radius" : 6.35 * mm, "tangentPropagation" : true, "allowEdgeOverflow" : false});
        }
        {
            var Q0;
            Q0=makeQuery(id+"F55.opExtrude","SWEPT_FACE",FACE,{"disambiguationData":[OSD([sQuery(id+"F54.wireOp",EDGE,"E46")])]});
            var Q1;
            Q1=makeQuery(id+"F56.opExtrude","SWEPT_FACE",FACE,{"disambiguationData":[OSD([sQuery(id+"F54.wireOp",EDGE,"E46")])]});
            var Q2;
            Q2=makeQuery(id+"F56.opExtrude","SWEPT_FACE",FACE,{"disambiguationData":[OSD([sQuery(id+"F54.wireOp",EDGE,"E48")])]});
            var Q3;
            Q3=makeQuery(id+"F55.opExtrude","SWEPT_FACE",FACE,{"disambiguationData":[OSD([sQuery(id+"F54.wireOp",EDGE,"E47.right")])]});
            var Q4;
            Q4=makeQuery(id+"F55.opExtrude","SWEPT_FACE",FACE,{"disambiguationData":[OSD([sQuery(id+"F54.wireOp",EDGE,"E56")])]});
            var Q5;
            Q5=makeQuery(id+"F56.opExtrude","SWEPT_FACE",FACE,{"disambiguationData":[OSD([sQuery(id+"F54.wireOp",EDGE,"E56")])]});
            var Q6;
            Q6=makeQuery(id+"F56.opExtrude","SWEPT_FACE",FACE,{"disambiguationData":[OSD([sQuery(id+"F54.wireOp",EDGE,"E52")])]});
            var Q7;
            Q7=makeQuery(id+"F56.opExtrude","SWEPT_FACE",FACE,{"disambiguationData":[OSD([sQuery(id+"F54.wireOp",EDGE,"E47.left")])]});
            var Q8;
            Q8=makeQuery(id+"F55.opExtrude","SWEPT_FACE",FACE,{"disambiguationData":[OSD([sQuery(id+"F54.wireOp",EDGE,"E57")])]});
            var Q9;
            Q9=makeQuery(id+"F56.opExtrude","SWEPT_FACE",FACE,{"disambiguationData":[OSD([sQuery(id+"F54.wireOp",EDGE,"E54")])]});
            fillet(context, id + "F58", {"entities" : qUnion([Q0, Q1, Q2, Q3, Q4, Q5, Q6, Q7, Q8, Q9]), "radius" : 0.76 * mm, "tangentPropagation" : true, "allowEdgeOverflow" : false});
        }
        {
            var Q0;
            Q0=makeQuery(id+"F56.opExtrude","SWEPT_FACE",FACE,{"disambiguationData":[OSD([sQuery(id+"F54.wireOp",EDGE,"E45.left")])]});
            var sketch = newSketch(context, id + "F59", { "sketchPlane" : qUnion([Q0])});
            skCircle(sketch, "E65", {"center": v(12.7, 0) * mm, "radius": 3.18 * mm});
            skSolve(sketch);
        }
        {
            var Q0;
            Q0 = qSketchRegion(id + "F59", true);
            extrude(context, id + "F60", {"entities" : qUnion([Q0]), "operationType" : NewBodyOperationType.REMOVE, "oppositeDirection" : true, "depth" : 25.4 * mm});
        }
        {
            var Q0;
            Q0=makeQuery(id+"F55.opExtrude","SWEPT_FACE",FACE,{"disambiguationData":[OSD([sQuery(id+"F54.wireOp",EDGE,"E45.right")])]});
            var sketch = newSketch(context, id + "F61", { "sketchPlane" : qUnion([Q0])});
            skCircle(sketch, "E66", {"center": v(-12.7, 0) * mm, "radius": 2.8 * mm});
            skSolve(sketch);
        }
        {
            var Q0;
            Q0 = qSketchRegion(id + "F61", true);
            extrude(context, id + "F62", {"entities" : qUnion([Q0]), "operationType" : NewBodyOperationType.REMOVE, "oppositeDirection" : true, "depth" : 50.8 * mm});
        }
        {
            var Q0;
            Q0=makeQuery(id+"F62.boolean.opBoolean","COPY",FACE,{"derivedFrom":makeQuery(id+"F62.opExtrude","SWEPT_FACE",FACE,{"disambiguationData":[OSD([sQuery(id+"F61.wireOp",EDGE,"E66")])]})});
            chamfer(context, id + "F63", {"entities" : qUnion([Q0]), "width" : 0.76 * mm, "tangentPropagation" : true});
        }
        {
            var Q0;
            Q0=makeQuery(id+"F56.opExtrude","SWEPT_FACE",FACE,{"disambiguationData":[OSD([sQuery(id+"F54.wireOp",EDGE,"E45.left")])]});
            chamfer(context, id + "F64", {"entities" : qUnion([Q0]), "width" : 2.54 * mm, "tangentPropagation" : true});
        }
        {
            var Q0;
            Q0=makeQuery(id+"F60.boolean.opBoolean","COPY",FACE,{"derivedFrom":makeQuery(id+"F60.opExtrude","SWEPT_FACE",FACE,{"disambiguationData":[OSD([sQuery(id+"F59.wireOp",EDGE,"E65")])]})});
            chamfer(context, id + "F65", {"entities" : qUnion([Q0]), "width" : 0.5 * mm, "tangentPropagation" : true});
        }
        {
            var Q0;
            Q0=makeQuery(id+"F56.opExtrude","SWEPT_FACE",FACE,{"disambiguationData":[OSD([sQuery(id+"F54.wireOp",EDGE,"E60.trimOffspring")])]});
            var sketch = newSketch(context, id + "F66", { "sketchPlane" : qUnion([Q0])});
            skLineSegment(sketch, "E67.bottom", {"start": v(-35.67, 43.03) * mm, "end": v(13.09, 43.03) * mm});
            skLineSegment(sketch, "E67.top", {"start": v(-35.67, -15.87) * mm, "end": v(13.09, -15.87) * mm});
            skLineSegment(sketch, "E67.left", {"start": v(-35.67, 43.03) * mm, "end": v(-35.67, -15.87) * mm});
            skLineSegment(sketch, "E67.right", {"start": v(13.09, 43.03) * mm, "end": v(13.09, -15.87) * mm});
            skSolve(sketch);
        }
        {
            var Q0;
            Q0 = qSketchRegion(id + "F66", true);
            extrude(context, id + "F67", {"entities" : qUnion([Q0]), "operationType" : NewBodyOperationType.REMOVE, "oppositeDirection" : true, "depth" : 0.25 * mm});
        }
        {
            var Q0;
            Q0=makeQuery(id+"F55.opExtrude","SWEPT_FACE",FACE,{"disambiguationData":[OSD([sQuery(id+"F54.wireOp",EDGE,"E60.trimOffspring")])]});
            var sketch = newSketch(context, id + "F68", { "sketchPlane" : qUnion([Q0])});
            skLineSegment(sketch, "E68.bottom", {"start": v(-8.18, 42.38) * mm, "end": v(36.65, 42.38) * mm});
            skLineSegment(sketch, "E68.top", {"start": v(-8.18, -15.87) * mm, "end": v(36.65, -15.87) * mm});
            skLineSegment(sketch, "E68.left", {"start": v(-8.18, 42.38) * mm, "end": v(-8.18, -15.87) * mm});
            skLineSegment(sketch, "E68.right", {"start": v(36.65, 42.38) * mm, "end": v(36.65, -15.87) * mm});
            skSolve(sketch);
        }
        {
            var Q0;
            Q0 = qSketchRegion(id + "F68", true);
            extrude(context, id + "F69", {"entities" : qUnion([Q0]), "operationType" : NewBodyOperationType.REMOVE, "oppositeDirection" : true, "depth" : 0.25 * mm});
        }
        {
            var Q0;
            {var subQ0=sQuery(id+"F54.wireOp",EDGE,"E45.bottom");Q0=makeQuery(id+"F67.boolean.opBoolean","COPY",FACE,{"disambiguationData":[TD([makeQuery(id+"F56.opExtrude","SWEPT_FACE",FACE,{"disambiguationData":[OSD([subQ0])]})])],"derivedFrom":makeQuery(id+"F67.opExtrude","CAP_FACE",FACE,{"disambiguationData":[OSD([sQuery(id+"F66.wireOp",EDGE,"E67.bottom"),sQuery(id+"F66.wireOp",EDGE,"E67.top"),sQuery(id+"F66.wireOp",EDGE,"E67.left"),sQuery(id+"F66.wireOp",EDGE,"E67.right")])],"isStart":false})});}
            var Q1;
            {var subQ2=sQuery(id+"F54.wireOp",EDGE,"E56");Q1=makeQuery(id+"F67.boolean.opBoolean","COPY",FACE,{"disambiguationData":[TD([makeQuery(id+"F58.opFillet","BLEND_FACE",FACE,{"disambiguationData":[OSD([subQ2]),TDD([makeQuery(id+"F56.opExtrude","CAP_EDGE",EDGE,{"disambiguationData":[OSD([subQ2])],"isStart":true})])]})])],"derivedFrom":makeQuery(id+"F67.opExtrude","CAP_FACE",FACE,{"disambiguationData":[OSD([sQuery(id+"F66.wireOp",EDGE,"E67.bottom"),sQuery(id+"F66.wireOp",EDGE,"E67.top"),sQuery(id+"F66.wireOp",EDGE,"E67.left"),sQuery(id+"F66.wireOp",EDGE,"E67.right")])],"isStart":false})});}
            var Q2;
            Q2=makeQuery(id+"F56.opExtrude","SWEPT_FACE",FACE,{"disambiguationData":[OSD([sQuery(id+"F54.wireOp",EDGE,"E47.left")])]});
            var Q3;
            {var subQ3=sQuery(id+"F54.wireOp",EDGE,"E45.bottom");Q3=makeQuery(id+"F69.boolean.opBoolean","COPY",FACE,{"disambiguationData":[TD([makeQuery(id+"F55.opExtrude","SWEPT_FACE",FACE,{"disambiguationData":[OSD([subQ3])]})])],"derivedFrom":makeQuery(id+"F69.opExtrude","CAP_FACE",FACE,{"disambiguationData":[OSD([sQuery(id+"F68.wireOp",EDGE,"E68.bottom"),sQuery(id+"F68.wireOp",EDGE,"E68.top"),sQuery(id+"F68.wireOp",EDGE,"E68.left"),sQuery(id+"F68.wireOp",EDGE,"E68.right")])],"isStart":false})});}
            var Q4;
            {var subQ6=sQuery(id+"F54.wireOp",EDGE,"E56");Q4=makeQuery(id+"F69.boolean.opBoolean","COPY",FACE,{"disambiguationData":[TD([makeQuery(id+"F58.opFillet","BLEND_FACE",FACE,{"disambiguationData":[OSD([subQ6]),TDD([makeQuery(id+"F55.opExtrude","CAP_EDGE",EDGE,{"disambiguationData":[OSD([subQ6])],"isStart":true})])]})])],"derivedFrom":makeQuery(id+"F69.opExtrude","CAP_FACE",FACE,{"disambiguationData":[OSD([sQuery(id+"F68.wireOp",EDGE,"E68.bottom"),sQuery(id+"F68.wireOp",EDGE,"E68.top"),sQuery(id+"F68.wireOp",EDGE,"E68.left"),sQuery(id+"F68.wireOp",EDGE,"E68.right")])],"isStart":false})});}
            var Q5;
            Q5=makeQuery(id+"F55.opExtrude","SWEPT_FACE",FACE,{"disambiguationData":[OSD([sQuery(id+"F54.wireOp",EDGE,"E47.right")])]});
            var Q6;
            Q6=makeQuery(id+"F55.opExtrude","SWEPT_FACE",FACE,{"disambiguationData":[OSD([sQuery(id+"F54.wireOp",EDGE,"E57")])]});
            fillet(context, id + "F70", {"entities" : qUnion([Q0, Q1, Q2, Q3, Q4, Q5, Q6]), "radius" : 0.5 * mm, "tangentPropagation" : true, "allowEdgeOverflow" : false});
        }
    });
